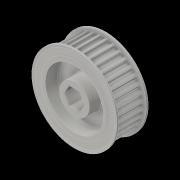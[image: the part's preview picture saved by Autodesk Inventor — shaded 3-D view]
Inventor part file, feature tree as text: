
AUTODESK INVENTOR PART (.ipt)
format: ipt  version: 2016 (Build 200138000, 138)  size: 1,025,024 bytes
history: native  units: in
note: dims shown in document units (in); Inventor stores cm internally (conversion verified against a paired STEP export)
features: mirror x1
ambient origin geometry x8: Origin, YZ Plane, XZ Plane, XY Plane, X Axis, Y Axis, Z Axis, Center Point
bodies: Solid1 (feature_tree)
feature tree (1):
  mirror  "Mirror1"
